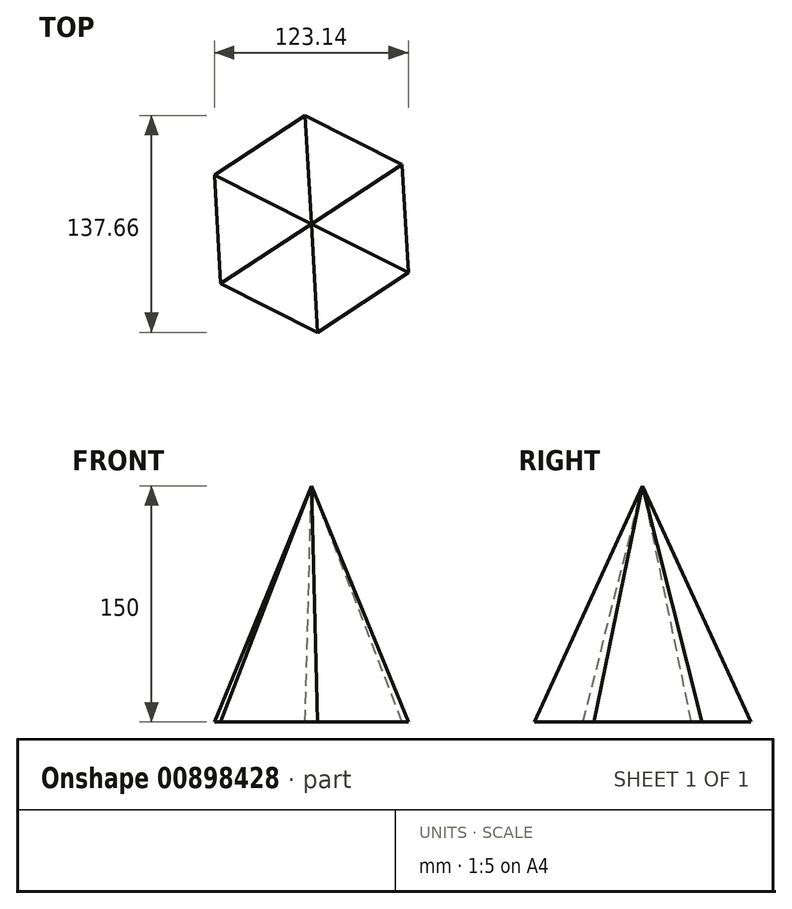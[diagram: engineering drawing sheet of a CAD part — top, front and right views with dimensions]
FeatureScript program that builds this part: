
annotation { "Feature Type Name" : "Feature", "Feature Type Description" : "" }
export const myFeature = defineFeature(function(context is Context, id is Id, definition is map)
    precondition{}
    {
        {
            var Q0;
            Q0=qCreatedBy(makeId("Top.planeOp"),FACE);
            var sketch = newSketch(context, id + "F0", { "sketchPlane" : qUnion([Q0])});
            skCircle(sketch, "E0.cCircle", {"center": v(0, 0) * mm, "radius": 68.94 * mm, "construction": true});
            skLineSegment(sketch, "E0.0", {"start": v(57.65, 37.82) * mm, "end": v(61.57, -31.01) * mm});
            skLineSegment(sketch, "E0.1", {"start": v(61.57, -31.01) * mm, "end": v(3.93, -68.83) * mm});
            skLineSegment(sketch, "E0.2", {"start": v(3.93, -68.83) * mm, "end": v(-57.65, -37.82) * mm});
            skLineSegment(sketch, "E0.3", {"start": v(-57.65, -37.82) * mm, "end": v(-61.57, 31.01) * mm});
            skLineSegment(sketch, "E0.4", {"start": v(-61.57, 31.01) * mm, "end": v(-3.93, 68.83) * mm});
            skLineSegment(sketch, "E0.5", {"start": v(-3.93, 68.83) * mm, "end": v(57.65, 37.82) * mm});
            skSolve(sketch);
        }
        {
            var Q0;
            Q0=qCreatedBy(makeId("Top.planeOp"),FACE);
            cPlane(context, id + "F1", {"entities" : qUnion([Q0]), "cplaneType" : CPlaneType.OFFSET, "offset" : 150 * mm, "width" : 150 * mm, "height" : 150 * mm});
        }
        {
            var Q0;
            Q0=qCreatedBy(id+"F1.planeOp",FACE);
            var sketch = newSketch(context, id + "F2", { "sketchPlane" : qUnion([Q0])});
            skPoint(sketch, "E1", {"position": v(0, 0) * mm});
            skSolve(sketch);
        }
        {
            var Q0;
            Q0=makeQuery(id+"F0.imprint","IMPRINT",FACE,{"disambiguationData":[TD([[makeQuery(id+"F0.imprint","IMPRINT",EDGE,{"derivedFrom":sQuery(id+"F0.wireOp",EDGE,"E0.0")}),-1.0]])]});
            var Q1;
            Q1=sQuery(id+"F2.wireOp",VERTEX,"E1");
            loft(context, id + "F3", {"sheetProfilesArray" : [{ "sheetProfileEntities" : qUnion([Q0]) }, { "sheetProfileEntities" : qUnion([Q1]) }]});
        }
    });
